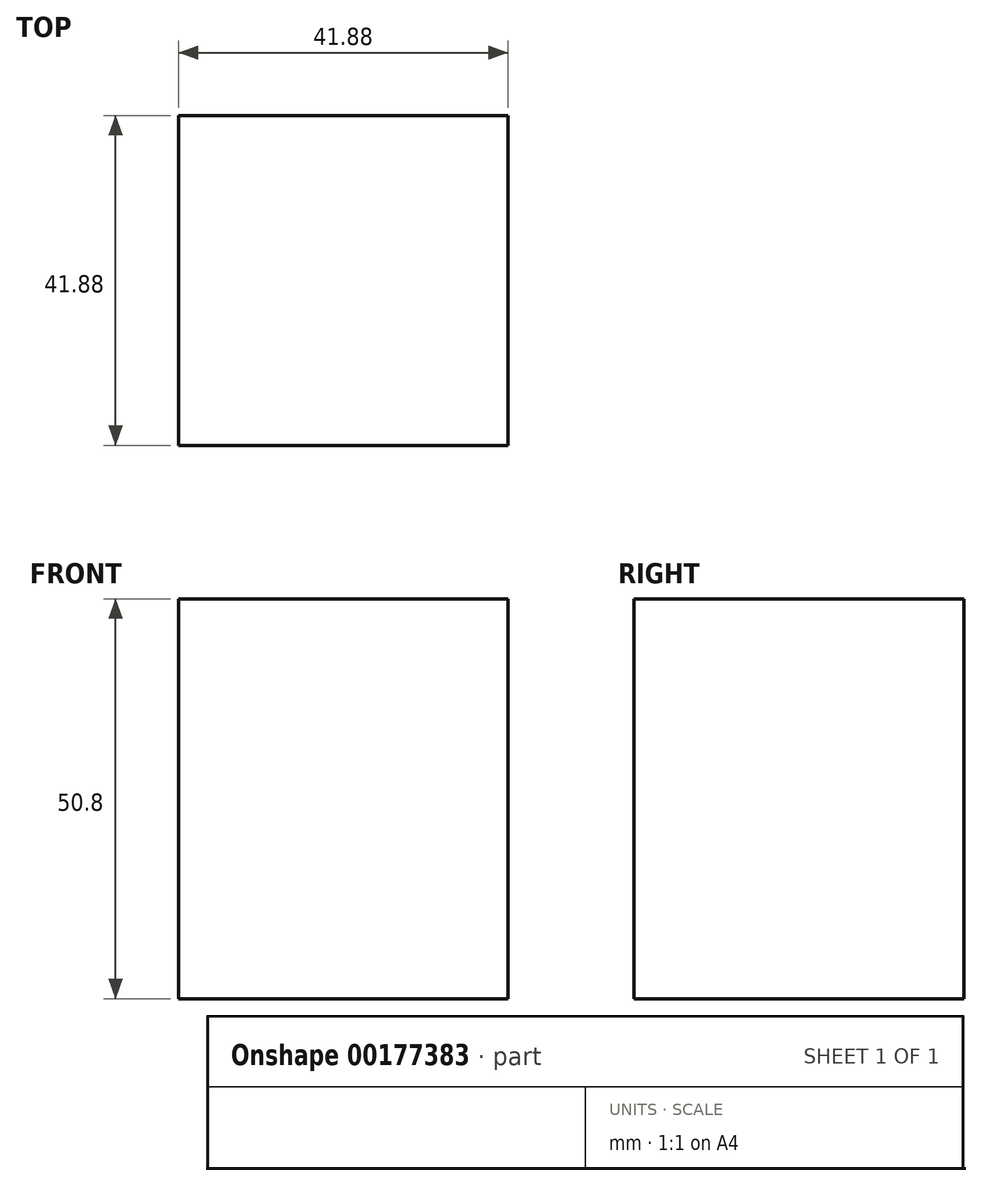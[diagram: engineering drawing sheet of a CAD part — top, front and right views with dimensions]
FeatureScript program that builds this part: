
annotation { "Feature Type Name" : "Feature", "Feature Type Description" : "" }
export const myFeature = defineFeature(function(context is Context, id is Id, definition is map)
    precondition{}
    {
        {
            var Q0;
            Q0=qCreatedBy(makeId("Top.planeOp"),FACE);
            var sketch = newSketch(context, id + "F0", { "sketchPlane" : qUnion([Q0])});
            skLineSegment(sketch, "E0.bottom", {"start": v(20.94, 20.94) * mm, "end": v(-20.94, 20.94) * mm});
            skLineSegment(sketch, "E0.top", {"start": v(20.94, -20.94) * mm, "end": v(-20.94, -20.94) * mm});
            skLineSegment(sketch, "E0.left", {"start": v(20.94, 20.94) * mm, "end": v(20.94, -20.94) * mm});
            skLineSegment(sketch, "E0.right", {"start": v(-20.94, 20.94) * mm, "end": v(-20.94, -20.94) * mm});
            skPoint(sketch, "E0.middle", {"position": v(0, 0) * mm});
            skSolve(sketch);
        }
        {
            var Q0;
            Q0=makeQuery(id+"F0.imprint","IMPRINT",FACE,{"disambiguationData":[TD([[makeQuery(id+"F0.imprint","IMPRINT",EDGE,{"derivedFrom":sQuery(id+"F0.wireOp",EDGE,"E0.bottom")}),1.0]])]});
            extrude(context, id + "F1", {"entities" : qUnion([Q0]), "depth" : 50.8 * mm});
        }
    });
